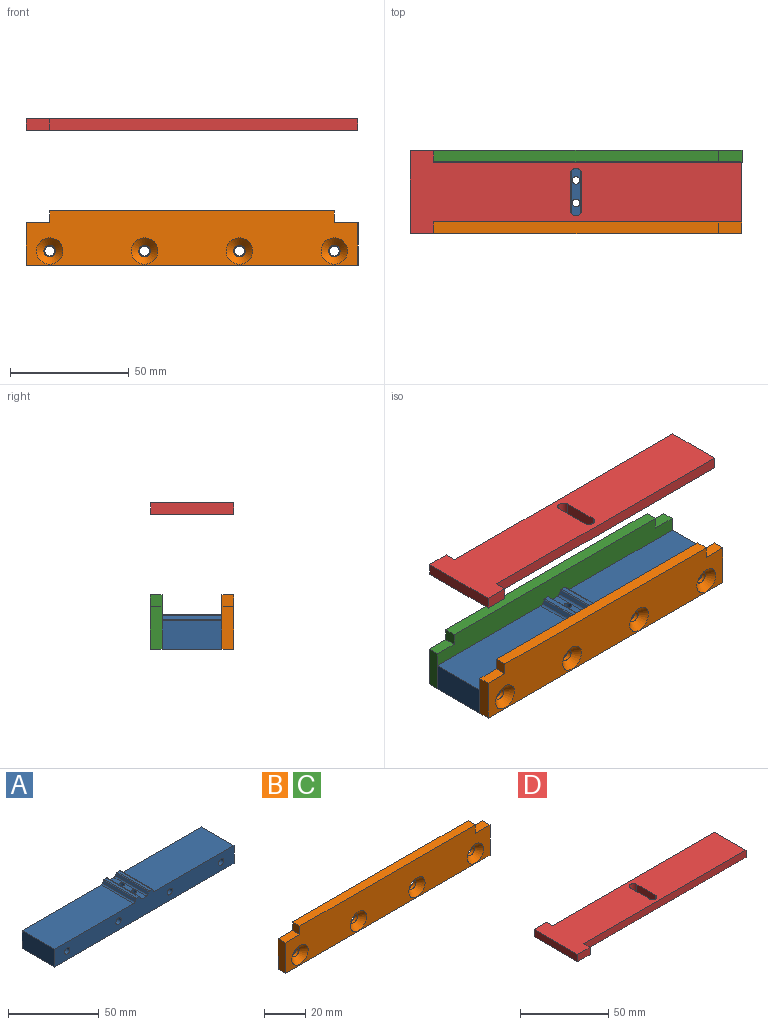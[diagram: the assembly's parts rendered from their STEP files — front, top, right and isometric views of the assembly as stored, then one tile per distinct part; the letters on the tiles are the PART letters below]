
ASSEMBLY  parts=4 mates=3
PART A: 28 faces, bbox 140x25.3x14.5 mm
  f0: plane 25.3x12mm, normal (-1,0,0), area 303.6mm2, adj f1,f11,f12,f13
  f1: plane 140x25.3mm, normal (0,0,-1), area 3525.9mm2, adj f0,f2,f12,f13,f22,f23
  f2: plane 25.3x12mm, normal (1,0,0), area 303.6mm2, adj f1,f3,f12,f13
  f3: plane 61.7x25.3mm, normal (0,0,1), area 1561.1mm2, adj f2,f12,f13,f18
  f4: plane 25.3x1.43mm, normal (0.91,0,0.42), area 40mm2, adj f12,f13,f14,f18
  f5: plane 25.3x1.9mm, normal (0,0,1), area 48.2mm2, adj f12,f13,f14,f15
  f6: plane 25.3x1.43mm, normal (-0.91,0,0.42), area 40mm2, adj f12,f13,f15,f19
  f7: plane 25.3x3.41mm, normal (0,0,1), area 70.1mm2, adj f12,f13,f19,f20,f22,f23
  f8: plane 25.3x1.43mm, normal (0.91,0,0.42), area 40mm2, adj f12,f13,f16,f20
  f9: plane 25.3x1.9mm, normal (0,0,1), area 48.2mm2, adj f12,f13,f16,f17
  f10: plane 25.3x1.43mm, normal (-0.91,0,0.42), area 40mm2, adj f12,f13,f17,f21
  f11: plane 61.7x25.3mm, normal (0,0,1), area 1561.1mm2, adj f0,f12,f13,f21
  f12: plane 140x14.5mm, normal (0,-1,0), area 1644.1mm2, adj f0,f1,f2,f3,f4,f5,f6,f7
  f13: plane 140x14.5mm, normal (0,1,0), area 1644.1mm2, adj f0,f1,f2,f3,f4,f5,f6,f7
  f14: cylinder r=0.6mm len=25.3mm, axis (0,1,0), area 17.2mm2, adj f4,f5,f12,f13
  f15: cylinder r=0.6mm len=25.3mm, axis (0,1,0), area 17.2mm2, adj f5,f6,f12,f13
  f16: cylinder r=0.6mm len=25.3mm, axis (0,1,0), area 17.2mm2, adj f8,f9,f12,f13
  f17: cylinder r=0.6mm len=25.3mm, axis (0,1,0), area 17.2mm2, adj f9,f10,f12,f13
  f18: cylinder r=1.25mm len=25.3mm, axis (0,-1,0), area 35.9mm2, adj f3,f4,f12,f13
  f19: cylinder r=1.25mm len=25.3mm, axis (0,-1,0), area 35.9mm2, adj f6,f7,f12,f13
  f20: cylinder r=1.25mm len=25.3mm, axis (0,-1,0), area 35.9mm2, adj f7,f8,f12,f13
  f21: cylinder r=1.25mm len=25.3mm, axis (0,-1,0), area 35.9mm2, adj f10,f11,f12,f13
  f22: cylinder r=1.6mm len=12mm, axis (0,0,1), area 120.6mm2, adj f1,f7
  f23: cylinder r=1.6mm len=12mm, axis (0,0,1), area 120.6mm2, adj f1,f7
  f24: cylinder r=2.1mm len=25.3mm, axis (0,-1,0), area 333.8mm2, adj f12,f13
  f25: cylinder r=2.1mm len=25.3mm, axis (0,-1,0), area 333.8mm2, adj f12,f13
  f26: cylinder r=2.1mm len=25.3mm, axis (0,-1,0), area 333.8mm2, adj f12,f13
  f27: cylinder r=2.1mm len=25.3mm, axis (0,-1,0), area 333.8mm2, adj f12,f13
PART B: 18 faces, bbox 140x5x23 mm
  f0: plane 18x5mm, normal (-1,0,0), area 90mm2, adj f1,f7,f8,f9
  f1: plane 140x5mm, normal (0,0,-1), area 700mm2, adj f0,f2,f8,f9
  f2: plane 18x5mm, normal (1,0,0), area 90mm2, adj f1,f3,f8,f9
  f3: plane 10x5mm, normal (0,0,1), area 50mm2, adj f2,f4,f8,f9
  f4: plane 5x5mm, normal (1,0,0), area 25mm2, adj f3,f5,f8,f9
  f5: plane 120x5mm, normal (0,0,1), area 600mm2, adj f4,f6,f8,f9
  f6: plane 5x5mm, normal (-1,0,0), area 25mm2, adj f5,f7,f8,f9
  f7: plane 10x5mm, normal (0,0,1), area 50mm2, adj f0,f6,f8,f9
  f8: plane 140x23mm, normal (0,-1,0), area 2725.9mm2, adj f0,f1,f2,f3,f4,f5,f6,f7
  f9: plane 140x23mm, normal (0,1,0), area 3041.5mm2, adj f0,f1,f2,f3,f4,f5,f6,f7
  f10: cylinder r=2.5mm len=5mm, axis (0,-1,0), area 29.8mm2, adj f9,f11
  f11: cone r=2.5mm half-angle=45deg, axis (0,-1,0), area 111.6mm2, adj f8,f10
  f12: cylinder r=2.5mm len=5mm, axis (0,-1,0), area 29.8mm2, adj f9,f13
  f13: cone r=2.5mm half-angle=45deg, axis (0,-1,0), area 111.6mm2, adj f8,f12
  f14: cylinder r=2.5mm len=5mm, axis (0,-1,0), area 29.8mm2, adj f9,f15
  f15: cone r=2.5mm half-angle=45deg, axis (0,-1,0), area 111.6mm2, adj f8,f14
  f16: cylinder r=2.5mm len=5mm, axis (0,-1,0), area 29.8mm2, adj f9,f17
  f17: cone r=2.5mm half-angle=45deg, axis (0,-1,0), area 111.6mm2, adj f8,f16
PART C: same geometry as B
PART D: 14 faces, bbox 140x35x5 mm
  f0: plane 35x5mm, normal (-1,0,0), area 175mm2, adj f1,f11,f12,f13
  f1: plane 10x5mm, normal (0,-1,0), area 50mm2, adj f0,f2,f12,f13
  f2: plane 5x5mm, normal (1,0,0), area 25mm2, adj f1,f3,f12,f13
  f3: plane 130x5mm, normal (0,-1,0), area 650mm2, adj f2,f4,f12,f13
  f4: plane 25x5mm, normal (1,0,0), area 125mm2, adj f3,f5,f12,f13
  f5: plane 130x5mm, normal (0,1,0), area 650mm2, adj f4,f6,f12,f13
  f6: plane 5x5mm, normal (1,0,0), area 25mm2, adj f5,f11,f12,f13
  f7: cylinder r=2.5mm len=5mm, axis (0,0,-1), area 39.3mm2, adj f8,f10,f12,f13
  f8: plane 15x5mm, normal (-1,0,0), area 75mm2, adj f7,f9,f12,f13
  f9: cylinder r=2.5mm len=5mm, axis (0,0,-1), area 39.3mm2, adj f8,f10,f12,f13
  f10: plane 15x5mm, normal (1,0,0), area 75mm2, adj f7,f9,f12,f13
  f11: plane 10x5mm, normal (0,1,0), area 50mm2, adj f0,f6,f12,f13
  f12: plane 140x35mm, normal (0,0,1), area 3505.4mm2, adj f0,f1,f2,f3,f4,f5,f6,f7
  f13: plane 140x35mm, normal (0,0,-1), area 3505.4mm2, adj f0,f1,f2,f3,f4,f5,f6,f7
PLACE A t=(18.2,12.13,33.24)mm fixed
PLACE B t=(18.2,-13.17,33.24)mm
PLACE C rot(axis=(0,0,1),180deg) t=(158.2,12.13,33.24)mm
PLACE D t=(18.2,-18.17,90.08)mm
MATE fastened A.f27 <-> B.f16  axis (0,-1,0) through (28.2,-13.17,39.24)mm
MATE slider B.f5 <-> D.f12  axis (0,0,1) through (28.2,-18.17,56.24)mm
MATE fastened A.f27 <-> C.f10  axis (0,1,0) through (28.2,12.13,39.24)mm
